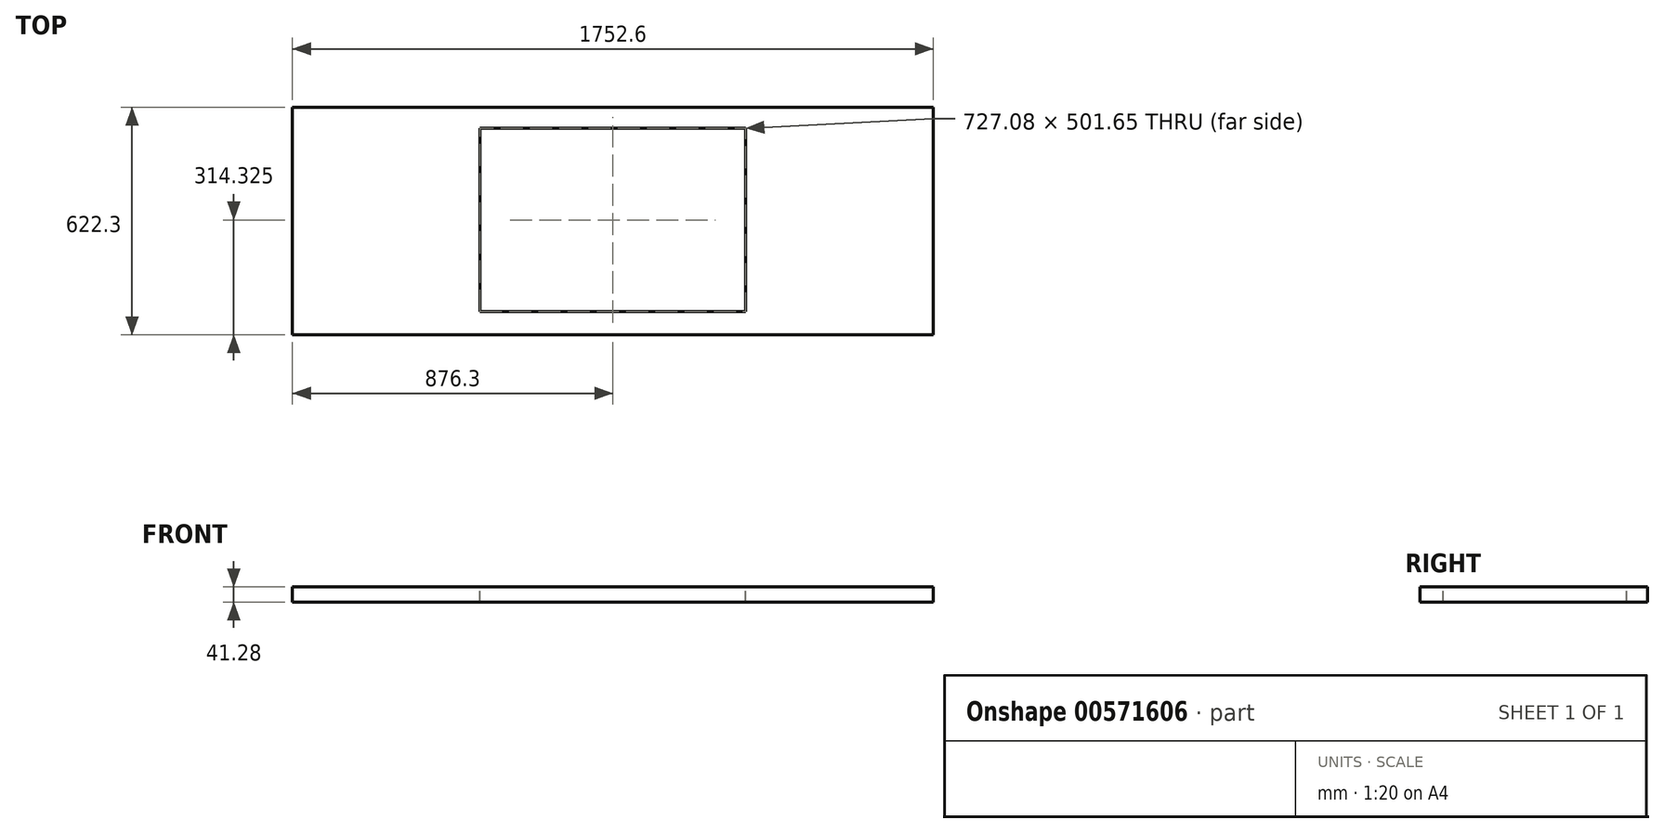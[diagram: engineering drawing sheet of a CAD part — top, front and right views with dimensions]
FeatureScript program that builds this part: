
annotation { "Feature Type Name" : "Feature", "Feature Type Description" : "" }
export const myFeature = defineFeature(function(context is Context, id is Id, definition is map)
    precondition{}
    {
        {
            var Q0;
            Q0=qCreatedBy(makeId("Top.planeOp"),FACE);
            var sketch = newSketch(context, id + "F0", { "sketchPlane" : qUnion([Q0])});
            skLineSegment(sketch, "E0.bottom", {"start": v(0, 0) * mm, "end": v(1752.6, 0) * mm});
            skLineSegment(sketch, "E0.top", {"start": v(0, 622.3) * mm, "end": v(1752.6, 622.3) * mm});
            skLineSegment(sketch, "E0.left", {"start": v(0, 0) * mm, "end": v(0, 622.3) * mm});
            skLineSegment(sketch, "E0.right", {"start": v(1752.6, 0) * mm, "end": v(1752.6, 622.3) * mm});
            skSolve(sketch);
        }
        {
            var Q0;
            Q0=makeQuery(id+"F0.imprint","IMPRINT",FACE,{"disambiguationData":[TD([[makeQuery(id+"F0.imprint","IMPRINT",EDGE,{"derivedFrom":sQuery(id+"F0.wireOp",EDGE,"E0.bottom")}),1.0]])]});
            extrude(context, id + "F1", {"entities" : qUnion([Q0]), "depth" : 41.27 * mm, "offsetDistance" : 25.4 * mm});
        }
        {
            var Q0;
            Q0=makeQuery(id+"F1.opExtrude","CAP_FACE",FACE,{"disambiguationData":[OSD([sQuery(id+"F0.wireOp",EDGE,"E0.bottom"),sQuery(id+"F0.wireOp",EDGE,"E0.top"),sQuery(id+"F0.wireOp",EDGE,"E0.left"),sQuery(id+"F0.wireOp",EDGE,"E0.right")])],"isStart":false});
            var sketch = newSketch(context, id + "F2", { "sketchPlane" : qUnion([Q0])});
            skLineSegment(sketch, "E1.bottom", {"start": v(1239.84, 63.5) * mm, "end": v(512.76, 63.5) * mm});
            skLineSegment(sketch, "E1.top", {"start": v(1239.84, 565.15) * mm, "end": v(512.76, 565.15) * mm});
            skLineSegment(sketch, "E1.left", {"start": v(1239.84, 63.5) * mm, "end": v(1239.84, 565.15) * mm});
            skLineSegment(sketch, "E1.right", {"start": v(512.76, 63.5) * mm, "end": v(512.76, 565.15) * mm});
            skPoint(sketch, "E1.middle", {"position": v(876.3, 314.32) * mm});
            skLineSegment(sketch, "E2", {"start": v(876.3, 622.3) * mm, "end": v(876.3, -1133.07) * mm, "construction": true});
            skSolve(sketch);
        }
        {
            var Q0;
            Q0=makeQuery(id+"F2.imprint","IMPRINT",FACE,{"disambiguationData":[TD([[makeQuery(id+"F2.imprint","IMPRINT",EDGE,{"derivedFrom":sQuery(id+"F2.wireOp",EDGE,"E1.bottom")}),-1.0]])]});
            extrude(context, id + "F3", {"entities" : qUnion([Q0]), "operationType" : NewBodyOperationType.REMOVE, "endBound" : BoundingType.THROUGH_ALL, "oppositeDirection" : true, "depth" : 25.4 * mm, "offsetDistance" : 25.4 * mm});
        }
    });
